# Revit family: BIMLIB_Кран_шаровой_В-Нр_РОСТерм
name_source: partatom
category: Арматура трубопроводов
revit_build: Autodesk Revit 2017 (Build: 20170118_1100(x64)
units: mm (PartAtom-declared; Revit-internal decimal feet)

## family parameters
Всегда вертикально = Да
На основе рабочей плоскости = Нет
Общий = Нет
При загрузке вырезать с полостями = Нет
Размер круглого соединителя = Использовать диаметр
Тип детали = Клапан - Вставляется

## types (1)
- ШКР ВР-HР
    ADSK_URL документации изделия = http://rostherm.ru
    ADSK_URL страницы изделия = http://rostherm.ru
    ADSK_Версия Revit = 2017
    ADSK_Единица измерения = шт.
    ADSK_Завод-изготовитель = Heizen
    ADSK_Материал = BIMLIB_Латунь_РТ
    ADSK_Обозначение = ГОСТ 21345-2005
    BL_BIM library = https://bimlib.pro
    URL = http://rostherm.ru
    Изготовитель = РОСТерм
    Описание = Кран шаровой выгодно отличается от аналогов компактностью. Небольшие габариты устройства позволяют использовать механизм для полного перекрывания потока рабочей среды на участке трубопроводной магистрали, где исключается любая дополнительная нагрузка (в промышленных системах охлаждения оборудования высокой мощности и тд).
    РТ_Максимальная температура = 160 °C
    РТ_Материал_Кран = BIMLIB_Красный_пластик_РТ
    РТ_Номинальное давление = 16.0 бары
    РТ_Рабочая температура = 120 °C
